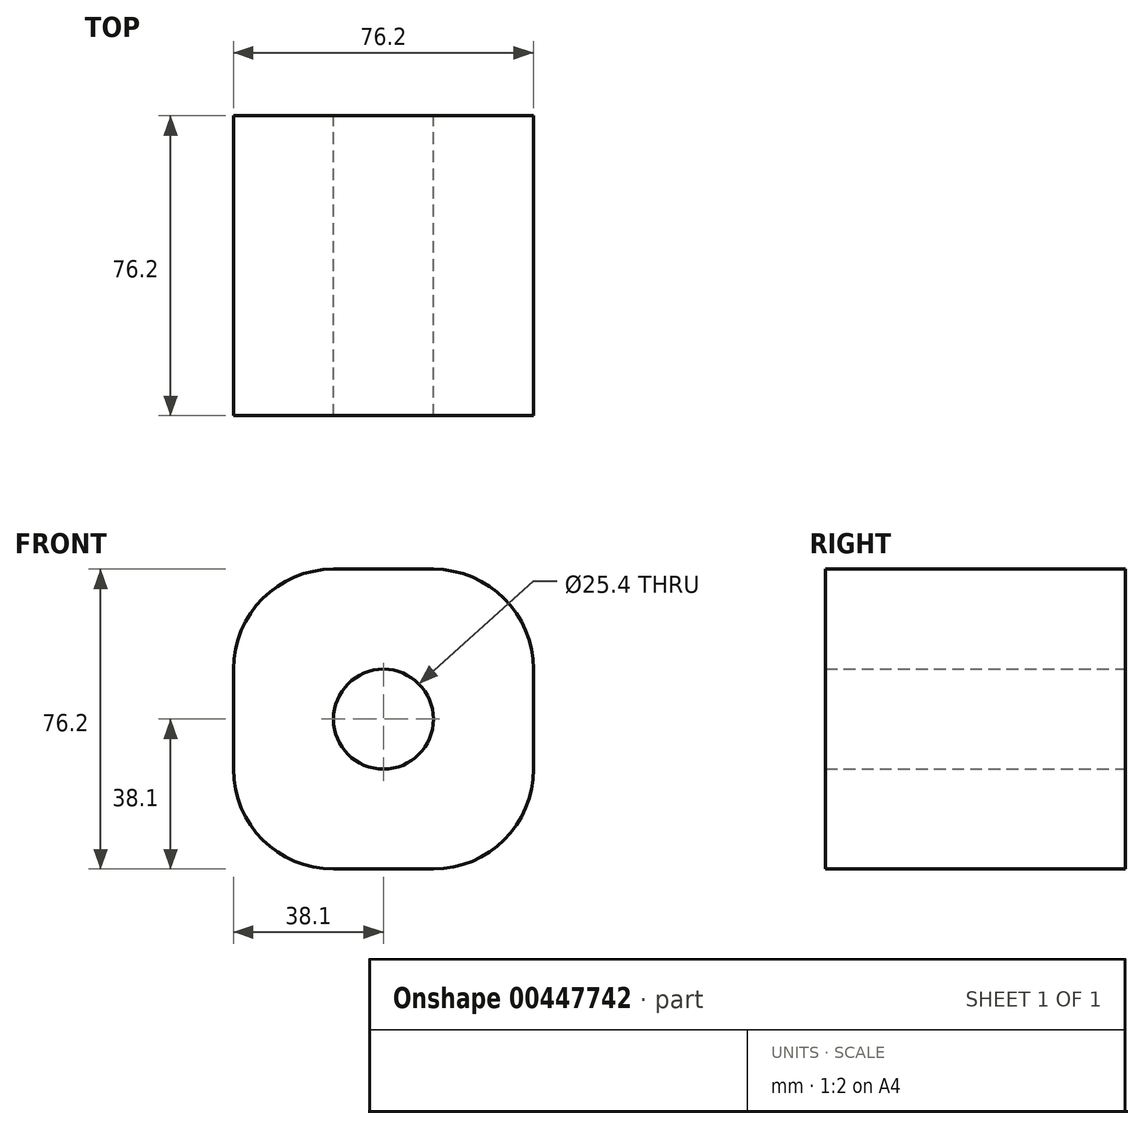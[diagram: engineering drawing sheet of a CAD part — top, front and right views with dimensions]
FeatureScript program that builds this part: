
annotation { "Feature Type Name" : "Feature", "Feature Type Description" : "" }
export const myFeature = defineFeature(function(context is Context, id is Id, definition is map)
    precondition{}
    {
        {
            var Q0;
            Q0=qCreatedBy(makeId("Front.planeOp"),FACE);
            var sketch = newSketch(context, id + "F0", { "sketchPlane" : qUnion([Q0])});
            skLineSegment(sketch, "E0.bottom", {"start": v(-12.7, 38.1) * mm, "end": v(12.7, 38.1) * mm});
            skLineSegment(sketch, "E0.top", {"start": v(-12.7, -38.1) * mm, "end": v(12.7, -38.1) * mm});
            skLineSegment(sketch, "E0.left", {"start": v(-38.1, 12.7) * mm, "end": v(-38.1, -12.7) * mm});
            skLineSegment(sketch, "E0.right", {"start": v(38.1, 12.7) * mm, "end": v(38.1, -12.7) * mm});
            skPoint(sketch, "E1.visualSharp", {"position": v(-38.1, 38.1) * mm});
            skArc(sketch, "E1.filletArc", {"start": v(-12.7, 38.1) * mm, "mid": v(-30.66, 30.66) * mm, "end": v(-38.1, 12.7) * mm});
            skPoint(sketch, "E2.visualSharp", {"position": v(38.1, 38.1) * mm});
            skArc(sketch, "E2.filletArc", {"start": v(38.1, 12.7) * mm, "mid": v(30.66, 30.66) * mm, "end": v(12.7, 38.1) * mm});
            skPoint(sketch, "E3.visualSharp", {"position": v(38.1, -38.1) * mm});
            skArc(sketch, "E3.filletArc", {"start": v(12.7, -38.1) * mm, "mid": v(30.66, -30.66) * mm, "end": v(38.1, -12.7) * mm});
            skPoint(sketch, "E4.visualSharp", {"position": v(-38.1, -38.1) * mm});
            skArc(sketch, "E4.filletArc", {"start": v(-38.1, -12.7) * mm, "mid": v(-30.66, -30.66) * mm, "end": v(-12.7, -38.1) * mm});
            skCircle(sketch, "E5", {"center": v(0, 0) * mm, "radius": 12.7 * mm});
            skSolve(sketch);
        }
        {
            var Q0;
            Q0=makeQuery(id+"F0.imprint","IMPRINT",FACE,{"disambiguationData":[TD([[makeQuery(id+"F0.imprint","IMPRINT",EDGE,{"derivedFrom":sQuery(id+"F0.wireOp",EDGE,"E0.bottom")}),-1.0]])]});
            extrude(context, id + "F1", {"entities" : qUnion([Q0]), "depth" : 76.2 * mm});
        }
    });
